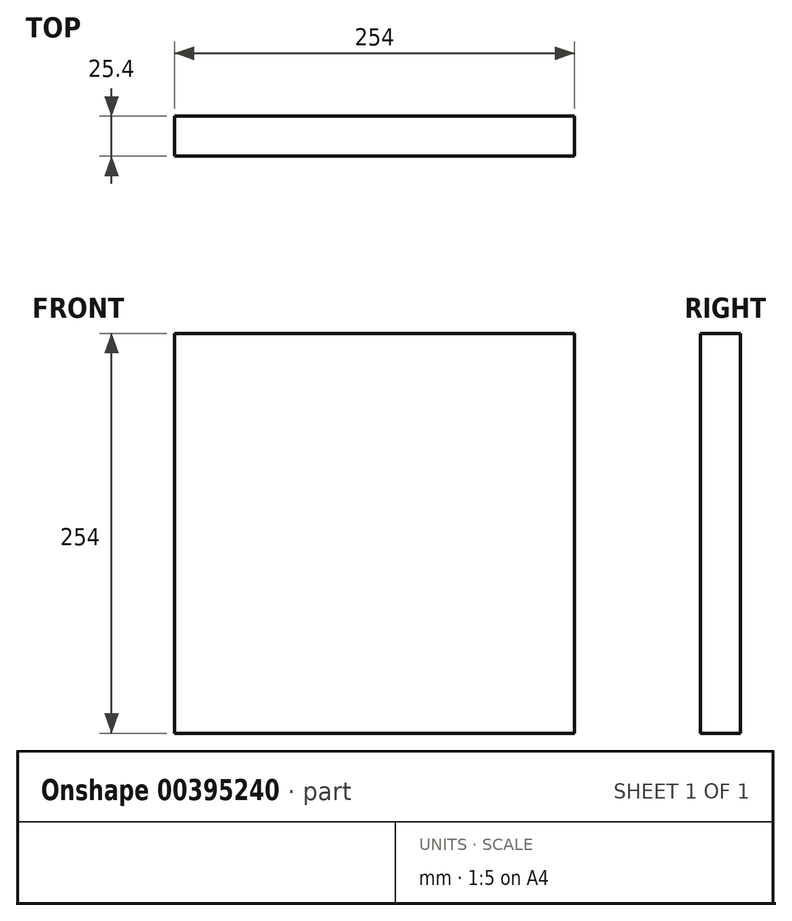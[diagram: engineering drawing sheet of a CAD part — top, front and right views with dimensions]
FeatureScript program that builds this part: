
annotation { "Feature Type Name" : "Feature", "Feature Type Description" : "" }
export const myFeature = defineFeature(function(context is Context, id is Id, definition is map)
    precondition{}
    {
        {
            var Q0;
            Q0=qCreatedBy(makeId("Front.planeOp"),FACE);
            var sketch = newSketch(context, id + "F0", { "sketchPlane" : qUnion([Q0])});
            skLineSegment(sketch, "E0.bottom", {"start": v(0, 0) * mm, "end": v(254, 0) * mm});
            skLineSegment(sketch, "E0.top", {"start": v(0, 254) * mm, "end": v(254, 254) * mm});
            skLineSegment(sketch, "E0.left", {"start": v(0, 0) * mm, "end": v(0, 254) * mm});
            skLineSegment(sketch, "E0.right", {"start": v(254, 0) * mm, "end": v(254, 254) * mm});
            skSolve(sketch);
        }
        {
            var Q0;
            Q0=makeQuery(id+"F0.imprint","IMPRINT",FACE,{"disambiguationData":[TD([[makeQuery(id+"F0.imprint","IMPRINT",EDGE,{"derivedFrom":sQuery(id+"F0.wireOp",EDGE,"E0.bottom")}),1.0]])]});
            extrude(context, id + "F1", {"entities" : qUnion([Q0]), "depth" : 25.4 * mm});
        }
    });
